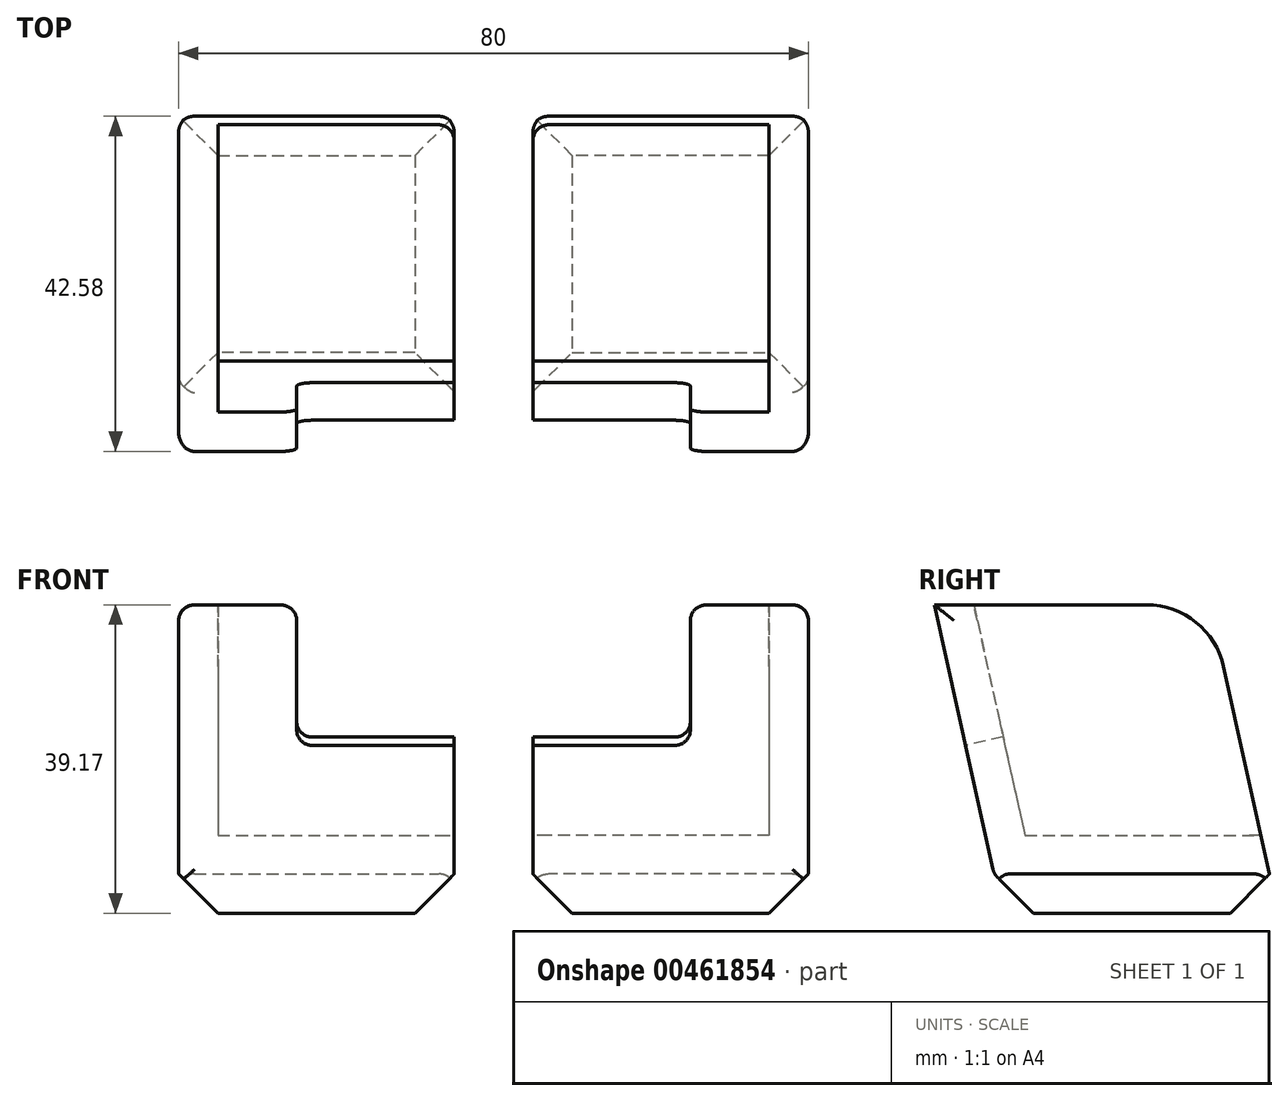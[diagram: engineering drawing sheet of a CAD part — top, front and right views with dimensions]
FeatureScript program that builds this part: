
annotation { "Feature Type Name" : "Feature", "Feature Type Description" : "" }
export const myFeature = defineFeature(function(context is Context, id is Id, definition is map)
    precondition{}
    {
        {
            var Q0;
            Q0=qCreatedBy(makeId("Right.planeOp"),FACE);
            var sketch = newSketch(context, id + "F0", { "sketchPlane" : qUnion([Q0])});
            skLineSegment(sketch, "E0", {"start": v(0, 0) * mm, "end": v(-7.58, 34.17) * mm});
            skLineSegment(sketch, "E1", {"start": v(-7.58, 34.17) * mm, "end": v(27.42, 34.17) * mm});
            skLineSegment(sketch, "E2", {"start": v(27.42, 34.17) * mm, "end": v(35, 0) * mm});
            skLineSegment(sketch, "E3", {"start": v(35, 0) * mm, "end": v(0, 0) * mm});
            skSolve(sketch);
        }
        {
            var Q0;
            Q0=makeQuery(id+"F0.imprint","IMPRINT",FACE,{"disambiguationData":[TD([[makeQuery(id+"F0.imprint","IMPRINT",EDGE,{"derivedFrom":sQuery(id+"F0.wireOp",EDGE,"E0")}),-1.0]])]});
            extrude(context, id + "F1", {"entities" : qUnion([Q0]), "oppositeDirection" : true, "depth" : 35 * mm});
        }
        {
            var Q0;
            Q0=makeQuery(id+"F1.opExtrude","CAP_FACE",FACE,{"disambiguationData":[OSD([sQuery(id+"F0.wireOp",EDGE,"E0"),sQuery(id+"F0.wireOp",EDGE,"E1"),sQuery(id+"F0.wireOp",EDGE,"E2"),sQuery(id+"F0.wireOp",EDGE,"E3")])],"isStart":true});
            var sketch = newSketch(context, id + "F2", { "sketchPlane" : qUnion([Q0])});
            skLineSegment(sketch, "E4", {"start": v(-2.58, 34.17) * mm, "end": v(3.92, 4.88) * mm});
            skLineSegment(sketch, "E5", {"start": v(3.92, 4.88) * mm, "end": v(33.92, 4.88) * mm});
            skLineSegment(sketch, "E6", {"start": v(33.92, 4.88) * mm, "end": v(27.42, 34.17) * mm});
            skLineSegment(sketch, "E7", {"start": v(27.42, 34.17) * mm, "end": v(-2.58, 34.17) * mm});
            skSolve(sketch);
        }
        {
            var Q0;
            Q0=makeQuery(id+"F2.imprint","IMPRINT",FACE,{"disambiguationData":[TD([[makeQuery(id+"F2.imprint","IMPRINT",EDGE,{"derivedFrom":sQuery(id+"F2.wireOp",EDGE,"E4")}),1.0]])]});
            extrude(context, id + "F3", {"entities" : qUnion([Q0]), "operationType" : NewBodyOperationType.REMOVE, "oppositeDirection" : true, "depth" : 30 * mm});
        }
        {
            var Q0;
            Q0=makeQuery(id+"F1.opExtrude","SWEPT_FACE",FACE,{"disambiguationData":[OSD([sQuery(id+"F0.wireOp",EDGE,"E0")])]});
            var sketch = newSketch(context, id + "F4", { "sketchPlane" : qUnion([Q0])});
            skLineSegment(sketch, "E8.bottom", {"start": v(0, 35) * mm, "end": v(-20, 35) * mm});
            skLineSegment(sketch, "E8.top", {"start": v(0, 16.72) * mm, "end": v(-20, 16.72) * mm});
            skLineSegment(sketch, "E8.left", {"start": v(0, 35) * mm, "end": v(0, 16.72) * mm});
            skLineSegment(sketch, "E8.right", {"start": v(-20, 35) * mm, "end": v(-20, 16.72) * mm});
            skSolve(sketch);
        }
        {
            var Q0;
            Q0=makeQuery(id+"F4.imprint","IMPRINT",FACE,{"disambiguationData":[TD([[makeQuery(id+"F4.imprint","IMPRINT",EDGE,{"derivedFrom":sQuery(id+"F4.wireOp",EDGE,"E8.bottom")}),-1.0]])]});
            extrude(context, id + "F5", {"entities" : qUnion([Q0]), "operationType" : NewBodyOperationType.REMOVE, "endBound" : BoundingType.THROUGH_ALL, "oppositeDirection" : true, "depth" : 25 * mm});
        }
        {
            var Q0;
            Q0=makeQuery(id+"F1.opExtrude","SWEPT_FACE",FACE,{"disambiguationData":[OSD([sQuery(id+"F0.wireOp",EDGE,"E1")])]});
            var sketch = newSketch(context, id + "F6", { "sketchPlane" : qUnion([Q0])});
            skLineSegment(sketch, "E9", {"start": v(-20, -7.58) * mm, "end": v(-20, -2.58) * mm});
            skSolve(sketch);
        }
        {
            var Q0;
            Q0=makeQuery(id+"F1.opExtrude","SWEPT_FACE",FACE,{"disambiguationData":[OSD([sQuery(id+"F0.wireOp",EDGE,"E3")])]});
            extrude(context, id + "F7", {"entities" : qUnion([Q0]), "operationType" : NewBodyOperationType.ADD, "depth" : 5 * mm});
        }
        {
            var Q0;
            Q0=makeQuery(id+"F7.opExtrude","CAP_FACE",FACE,{"disambiguationData":[OSD([sQuery(id+"F0.wireOp",EDGE,"E3")])],"isStart":false});
            chamfer(context, id + "F8", {"entities" : qUnion([Q0]), "width" : 5 * mm, "tangentPropagation" : true});
        }
        {
            var Q0;
            Q0=makeQuery(id+"F1.opExtrude","CAP_EDGE",EDGE,{"disambiguationData":[OSD([sQuery(id+"F0.wireOp",EDGE,"E1")])],"isStart":false});
            var Q1;
            Q1=makeQuery(id+"Ffm0TRoBl4BYz5a_1.boolean.opBoolean","COPY",EDGE,{"derivedFrom":makeQuery(id+"Ffm0TRoBl4BYz5a_1.opExtrude","CAP_EDGE",EDGE,{"disambiguationData":[OSD([sQuery(id+"F6.wireOp",EDGE,"E9")])],"isStart":true})});
            var Q2;
            Q2=makeQuery(id+"F5.boolean.opBoolean","COPY",EDGE,{"derivedFrom":makeQuery(id+"F5.opExtrude","SWEPT_EDGE",EDGE,{"disambiguationData":[OSD([sQuery(id+"F4.wireOp",EDGE,"E8.top"),sQuery(id+"F4.wireOp",EDGE,"E8.right")])]})});
            var Q3;
            Q3=makeQuery(id+"F5.boolean.opBoolean","COPY",EDGE,{"derivedFrom":makeQuery(id+"F5.opExtrude","SWEPT_EDGE",EDGE,{"disambiguationData":[OSD([sQuery(id+"F0.wireOp",EDGE,"E0"),sQuery(id+"F4.wireOp",EDGE,"E8.top"),sQuery(id+"F4.wireOp",EDGE,"E8.left")])]})});
            var Q4;
            Q4=makeQuery(id+"F1.opExtrude","CAP_EDGE",EDGE,{"disambiguationData":[OSD([sQuery(id+"F0.wireOp",EDGE,"E0")])],"isStart":false});
            var Q5;
            Q5=makeQuery(id+"F1.opExtrude","CAP_EDGE",EDGE,{"disambiguationData":[OSD([sQuery(id+"F0.wireOp",EDGE,"E2")])],"isStart":false});
            var Q6;
            {var subQ0=sQuery(id+"F0.wireOp",EDGE,"E0");Q6=makeQuery(id+"F8.opChamfer","BLEND_EDGE",EDGE,{"blendedFrom":[makeQuery(id+"F7.opExtrude","CAP_EDGE",EDGE,{"disambiguationData":[OSD([subQ0,sQuery(id+"F0.wireOp",EDGE,"E3")])],"isStart":false}),makeQuery(id+"F1.opExtrude","SWEPT_FACE",FACE,{"disambiguationData":[OSD([subQ0])]})],"blendedInto":[makeQuery(id+"F1.opExtrude","SWEPT_FACE",FACE,{"disambiguationData":[OSD([subQ0])]})]});}
            fillet(context, id + "F9", {"entities" : qUnion([Q0, Q1, Q2, Q3, Q4, Q5, Q6]), "radius" : 2 * mm, "tangentPropagation" : true, "allowEdgeOverflow" : false});
        }
        {
            var Q0;
            Q0=makeQuery(id+"F1.opExtrude","CAP_EDGE",EDGE,{"disambiguationData":[OSD([sQuery(id+"F0.wireOp",EDGE,"E2")])],"isStart":true});
            fillet(context, id + "F10", {"entities" : qUnion([Q0]), "radius" : 2 * mm, "tangentPropagation" : true, "allowEdgeOverflow" : false});
        }
        {
            var Q0;
            Q0=makeQuery(id+"F1.opExtrude","SWEPT_EDGE",EDGE,{"disambiguationData":[OSD([sQuery(id+"F0.wireOp",EDGE,"E1"),sQuery(id+"F0.wireOp",EDGE,"E2")])]});
            fillet(context, id + "F11", {"entities" : qUnion([Q0]), "radius" : 10 * mm, "tangentPropagation" : true, "allowEdgeOverflow" : false});
        }
        {
            var Q0;
            Q0=qCreatedBy(makeId("Right.planeOp"),FACE);
            cPlane(context, id + "F12", {"entities" : qUnion([Q0]), "cplaneType" : CPlaneType.OFFSET, "offset" : 5 * mm, "width" : 150 * mm, "height" : 150 * mm});
        }
        {
            var Q0;
            Q0=makeQuery(id+"F5.boolean.opBoolean","INTERSECT",EDGE,{"derivedFrom":[makeQuery(id+"F1.opExtrude","SWEPT_FACE",FACE,{"disambiguationData":[OSD([sQuery(id+"F0.wireOp",EDGE,"E1")])]}),makeQuery(id+"F5.opExtrude","SWEPT_FACE",FACE,{"disambiguationData":[OSD([sQuery(id+"F4.wireOp",EDGE,"E8.right")])]})]});
            fillet(context, id + "F13", {"entities" : qUnion([Q0]), "radius" : 2 * mm, "tangentPropagation" : true, "allowEdgeOverflow" : false});
        }
        {
            var Q0;
            Q0=makeQuery(id+"F1.opExtrude","SWEPT_BODY",BODY,{"disambiguationData":[OSD([sQuery(id+"F0.wireOp",EDGE,"E0"),sQuery(id+"F0.wireOp",EDGE,"E1"),sQuery(id+"F0.wireOp",EDGE,"E2"),sQuery(id+"F0.wireOp",EDGE,"E3")])]});
            var Q1;
            Q1=qCreatedBy(id+"F12.planeOp",FACE);
            mirror(context, id + "F14", {"entities" : qUnion([Q0]), "mirrorPlane" : qUnion([Q1])});
        }
    });
